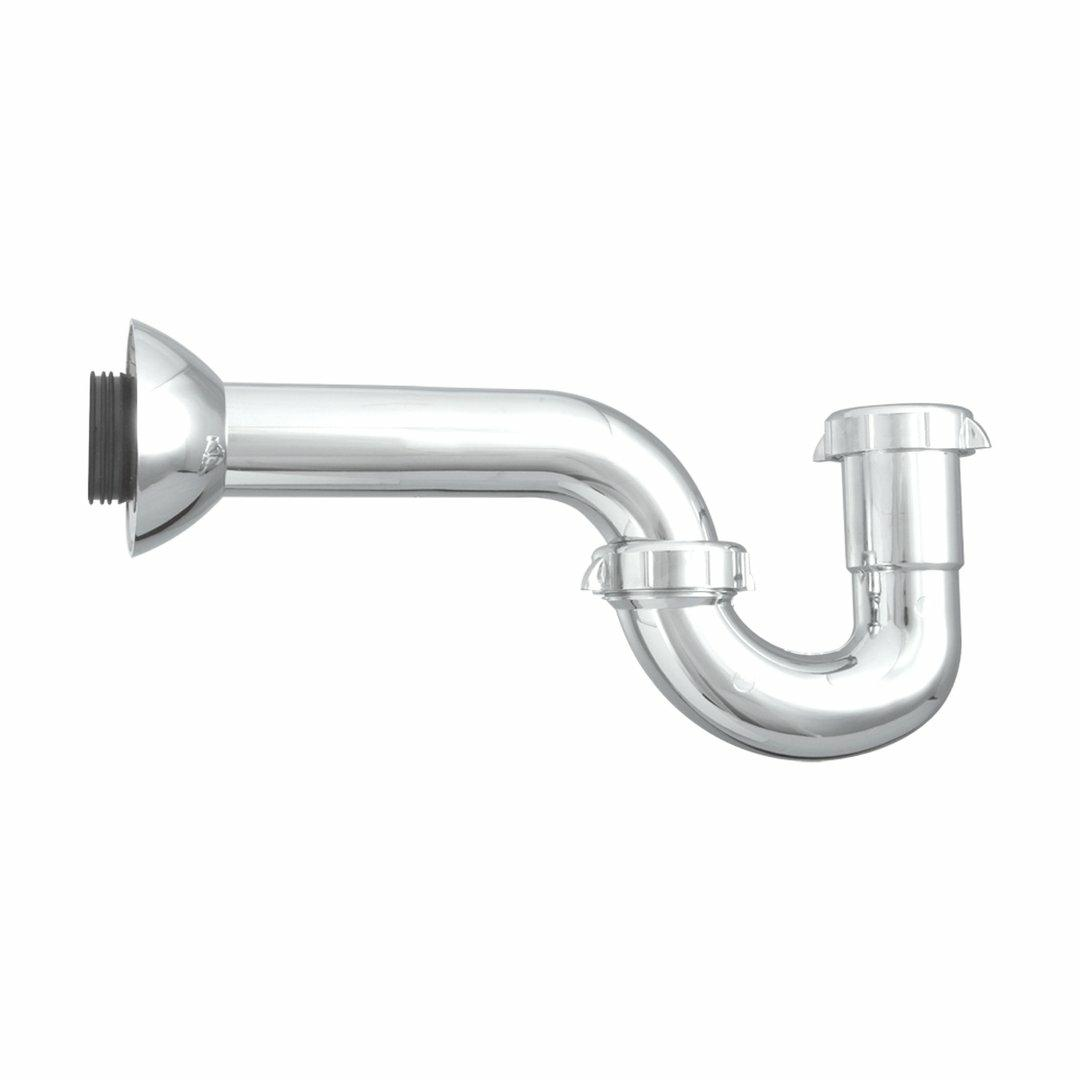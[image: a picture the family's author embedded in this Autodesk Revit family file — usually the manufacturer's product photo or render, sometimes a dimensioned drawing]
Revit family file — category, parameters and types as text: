
# Revit family: BIM_M1-3001-111
name_source: partatom
category: Aparatos sanitarios
units: mm (PartAtom-declared; Revit-internal decimal feet)

## family parameters
Activar corte en vistas = No
Anfitrión = Cara
Compartido = No
Corte con vacíos al cargar = No
Cota de conector redondo = Usar diámetro
Mantener orientación de anotación = No
Número OmniClass = 23.31.11.00
Punto de cálculo de habitación = No
Tipo de pieza = Normal

## types (1)
- M1-3001-111
    Acabado = Cepillado Brillante
    Alto = 17.5 mm  [stored 0.0574147 ft]
    Ancho = 100 mm  [stored 0.328084 ft]
    Conexión AC = Sí
    Conexión AF = Sí
    Conexión de residuos = No
    Conexión de ventilación = No
    Date Modified = 08-08-2025
    Descripción = Lavaplatos en acero
    Elevación por defecto = 0 mm  [stored 0 ft]
    Fabricante = Gricol
    Imagen de tipo = FOTO-LAVAPLATOS EN ACERO POCETA IZQUIERDA 100 x 50 cm.jpg
    Largo = 50 mm  [stored 0.164042 ft]
    Link Ficha Tecnica = https://infotecnica.gricol.com
    Material = Acero inoxidable
    Materiales del producto = Acero Inoxidable
    Modelo = M1-3001-111
    Nota clave = Lavaplatos con perforaciones para instalar grifería de 8"
    Product Name = Lavaplatos De Sobreponer Poceta Izquierda 100 X 50 Cm Con Complementos Para Mezclador
    Resistencia a Corrosión = Si
    Sitio web = https://www.gricol.com
    Tipo de Uso = Residencial
    URL = https://www.gricol.com

note: [stored X ft] marks values corroborated as IEEE doubles in the binary element streams (Revit-internal decimal feet)

## geometry (parser evidence)
native form markers: Blend x2, Sweep x12
no freeform markers — native parametric forms only
